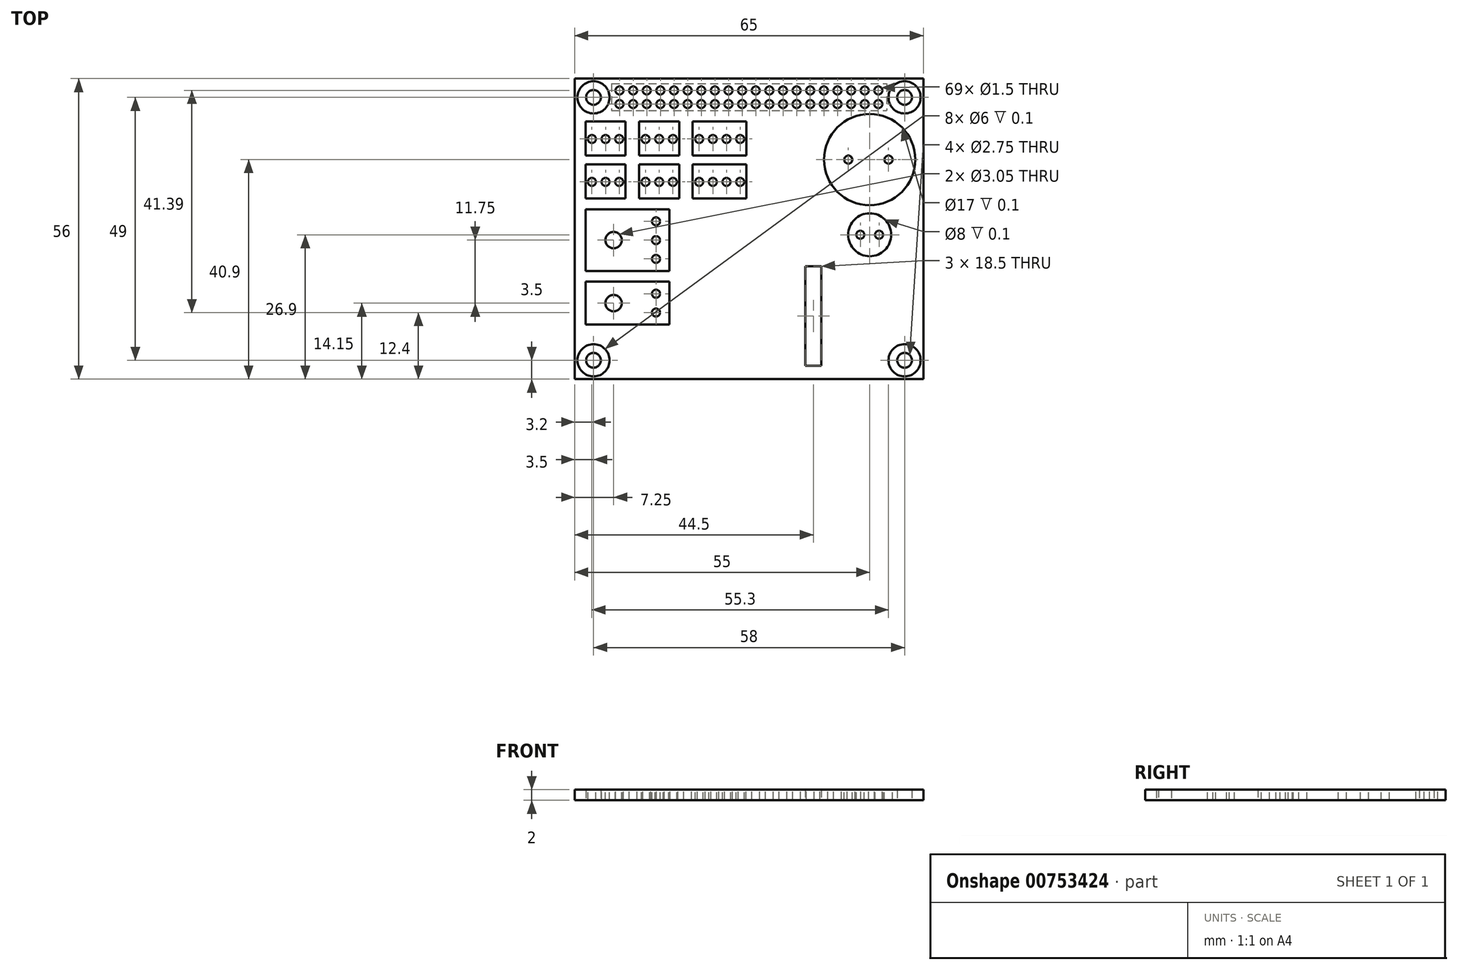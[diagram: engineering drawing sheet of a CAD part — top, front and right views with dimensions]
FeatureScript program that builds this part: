
annotation { "Feature Type Name" : "Feature", "Feature Type Description" : "" }
export const myFeature = defineFeature(function(context is Context, id is Id, definition is map)
    precondition{}
    {
        {
            var Q0;
            Q0=qCreatedBy(makeId("Top.planeOp"),FACE);
            var sketch = newSketch(context, id + "F0", { "sketchPlane" : qUnion([Q0])});
            skLineSegment(sketch, "E0.bottom", {"start": v(-32.5, 28) * mm, "end": v(52.5, 28) * mm});
            skLineSegment(sketch, "E0.top", {"start": v(-32.5, -28) * mm, "end": v(52.5, -28) * mm});
            skLineSegment(sketch, "E0.left", {"start": v(-32.5, 28) * mm, "end": v(-32.5, -28) * mm});
            skLineSegment(sketch, "E0.right", {"start": v(52.5, 28) * mm, "end": v(52.5, -28) * mm});
            skCircle(sketch, "E1", {"center": v(-29, 24.5) * mm, "radius": 1.38 * mm});
            skCircle(sketch, "E2", {"center": v(-29, -24.5) * mm, "radius": 1.38 * mm});
            skCircle(sketch, "E3", {"center": v(29, 24.5) * mm, "radius": 1.38 * mm});
            skCircle(sketch, "E4", {"center": v(29, -24.5) * mm, "radius": 1.38 * mm});
            skCircle(sketch, "E5", {"center": v(-29, -24.5) * mm, "radius": 3 * mm});
            skCircle(sketch, "E6", {"center": v(-29, 24.5) * mm, "radius": 3 * mm});
            skCircle(sketch, "E7", {"center": v(29, 24.5) * mm, "radius": 3 * mm});
            skCircle(sketch, "E8", {"center": v(29, -24.5) * mm, "radius": 3 * mm});
            skLineSegment(sketch, "E9", {"start": v(32.5, 28) * mm, "end": v(32.5, -28) * mm});
            skLineSegment(sketch, "E10.bottom", {"start": v(10.5, -7) * mm, "end": v(13.5, -7) * mm});
            skLineSegment(sketch, "E10.top", {"start": v(10.5, -25.5) * mm, "end": v(13.5, -25.5) * mm});
            skLineSegment(sketch, "E10.left", {"start": v(10.5, -7) * mm, "end": v(10.5, -25.5) * mm});
            skLineSegment(sketch, "E10.right", {"start": v(13.5, -7) * mm, "end": v(13.5, -25.5) * mm});
            skSolve(sketch);
        }
        {
            var Q0;
            {var subQ0=sQuery(id+"F0.wireOp",EDGE,"E0.left");Q0=makeQuery(id+"F0.imprint","IMPRINT",FACE,{"disambiguationData":[TD([[makeQuery(id+"F0.imprint","IMPRINT",EDGE,{"derivedFrom":subQ0}),1.0]])]});}
            extrude(context, id + "F1", {"entities" : qUnion([Q0]), "depth" : 1 * mm, "offsetDistance" : 25 * mm, "hasSecondDirection" : true, "secondDirectionOppositeDirection" : true, "secondDirectionDepth" : 1 * mm});
        }
        {
            var Q0;
            Q0=qCreatedBy(makeId("Top.planeOp"),FACE);
            var sketch = newSketch(context, id + "F2", { "sketchPlane" : qUnion([Q0])});
            skLineSegment(sketch, "E11.bottom", {"start": v(-32.5, 28) * mm, "end": v(52.5, 28) * mm});
            skLineSegment(sketch, "E11.top", {"start": v(-32.5, -28) * mm, "end": v(52.5, -28) * mm});
            skLineSegment(sketch, "E11.left", {"start": v(-32.5, 28) * mm, "end": v(-32.5, -28) * mm});
            skLineSegment(sketch, "E11.right", {"start": v(52.5, 28) * mm, "end": v(52.5, -28) * mm});
            skCircle(sketch, "E12", {"center": v(-29, 24.5) * mm, "radius": 1.38 * mm});
            skCircle(sketch, "E13", {"center": v(-29, -24.5) * mm, "radius": 1.38 * mm});
            skCircle(sketch, "E14", {"center": v(29, 24.5) * mm, "radius": 1.38 * mm});
            skCircle(sketch, "E15", {"center": v(29, -24.5) * mm, "radius": 1.38 * mm});
            skCircle(sketch, "E16", {"center": v(-29, -24.5) * mm, "radius": 3 * mm});
            skCircle(sketch, "E17", {"center": v(-29, 24.5) * mm, "radius": 3 * mm});
            skCircle(sketch, "E18", {"center": v(29, 24.5) * mm, "radius": 3 * mm});
            skCircle(sketch, "E19", {"center": v(29, -24.5) * mm, "radius": 3 * mm});
            skLineSegment(sketch, "E20", {"start": v(32.5, 28) * mm, "end": v(32.5, -28) * mm});
            skSolve(sketch);
        }
        {
            var Q0;
            Q0=makeQuery(id+"F2.imprint","IMPRINT",FACE,{"disambiguationData":[TD([[makeQuery(id+"F2.imprint","IMPRINT",EDGE,{"derivedFrom":sQuery(id+"F2.wireOp",EDGE,"E12")}),-1.0]])]});
            var Q1;
            Q1=makeQuery(id+"F2.imprint","IMPRINT",FACE,{"disambiguationData":[TD([[makeQuery(id+"F2.imprint","IMPRINT",EDGE,{"derivedFrom":sQuery(id+"F2.wireOp",EDGE,"E14")}),-1.0]])]});
            var Q2;
            Q2=makeQuery(id+"F2.imprint","IMPRINT",FACE,{"disambiguationData":[TD([[makeQuery(id+"F2.imprint","IMPRINT",EDGE,{"derivedFrom":sQuery(id+"F2.wireOp",EDGE,"E15")}),-1.0]])]});
            var Q3;
            Q3=makeQuery(id+"F2.imprint","IMPRINT",FACE,{"disambiguationData":[TD([[makeQuery(id+"F2.imprint","IMPRINT",EDGE,{"derivedFrom":sQuery(id+"F2.wireOp",EDGE,"E13")}),-1.0]])]});
            var Q4;
            Q4=makeQuery(id+"F1.opExtrude","CAP_FACE",FACE,{"disambiguationData":[OSD([sQuery(id+"F0.wireOp",EDGE,"E0.bottom"),sQuery(id+"F0.wireOp",EDGE,"E0.top"),sQuery(id+"F0.wireOp",EDGE,"E0.left"),sQuery(id+"F0.wireOp",EDGE,"E5"),sQuery(id+"F0.wireOp",EDGE,"E6"),sQuery(id+"F0.wireOp",EDGE,"E7"),sQuery(id+"F0.wireOp",EDGE,"E8"),sQuery(id+"F0.wireOp",EDGE,"E9")])],"isStart":false});
            var Q5;
            Q5=makeQuery(id+"F1.opExtrude","CAP_FACE",FACE,{"disambiguationData":[OSD([sQuery(id+"F0.wireOp",EDGE,"E0.bottom"),sQuery(id+"F0.wireOp",EDGE,"E0.top"),sQuery(id+"F0.wireOp",EDGE,"E0.left"),sQuery(id+"F0.wireOp",EDGE,"E5"),sQuery(id+"F0.wireOp",EDGE,"E6"),sQuery(id+"F0.wireOp",EDGE,"E7"),sQuery(id+"F0.wireOp",EDGE,"E8"),sQuery(id+"F0.wireOp",EDGE,"E9")])],"isStart":true});
            extrude(context, id + "F3", {"entities" : qUnion([Q0, Q1, Q2, Q3]), "operationType" : NewBodyOperationType.ADD, "endBound" : BoundingType.UP_TO_SURFACE, "depth" : 1.4 * mm, "endBoundEntityFace" : qUnion([Q4]), "hasOffset" : true, "offsetDistance" : 0.1 * mm, "hasSecondDirection" : true, "secondDirectionBound" : BoundingType.UP_TO_SURFACE, "secondDirectionOppositeDirection" : true, "secondDirectionDepth" : 1.4 * mm, "secondDirectionBoundEntityFace" : qUnion([Q5]), "hasSecondDirectionOffset" : true, "secondDirectionOffsetDistance" : 0.1 * mm});
        }
        {
            var Q0;
            Q0=makeQuery(id+"F1.opExtrude","CAP_FACE",FACE,{"disambiguationData":[OSD([sQuery(id+"F0.wireOp",EDGE,"E0.bottom"),sQuery(id+"F0.wireOp",EDGE,"E0.top"),sQuery(id+"F0.wireOp",EDGE,"E0.left"),sQuery(id+"F0.wireOp",EDGE,"E5"),sQuery(id+"F0.wireOp",EDGE,"E6"),sQuery(id+"F0.wireOp",EDGE,"E7"),sQuery(id+"F0.wireOp",EDGE,"E8"),sQuery(id+"F0.wireOp",EDGE,"E9"),sQuery(id+"F0.wireOp",EDGE,"E10.bottom"),sQuery(id+"F0.wireOp",EDGE,"E10.top"),sQuery(id+"F0.wireOp",EDGE,"E10.left"),sQuery(id+"F0.wireOp",EDGE,"E10.right")])],"isStart":false});
            var sketch = newSketch(context, id + "F4", { "sketchPlane" : qUnion([Q0])});
            skLineSegment(sketch, "E21.bottom", {"start": v(-30.5, 20) * mm, "end": v(-23.03, 20) * mm});
            skLineSegment(sketch, "E21.top", {"start": v(-30.5, 13.65) * mm, "end": v(-23.03, 13.65) * mm});
            skLineSegment(sketch, "E21.left", {"start": v(-30.5, 20) * mm, "end": v(-30.5, 13.65) * mm});
            skLineSegment(sketch, "E21.right", {"start": v(-23.03, 20) * mm, "end": v(-23.03, 13.65) * mm});
            skLineSegment(sketch, "E22.bottom", {"start": v(-30.5, 3.65) * mm, "end": v(-14.84, 3.65) * mm});
            skLineSegment(sketch, "E22.top", {"start": v(-30.5, -7.85) * mm, "end": v(-14.84, -7.85) * mm});
            skLineSegment(sketch, "E22.left", {"start": v(-30.5, 3.65) * mm, "end": v(-30.5, -7.85) * mm});
            skLineSegment(sketch, "E22.right", {"start": v(-14.84, 3.65) * mm, "end": v(-14.84, -7.85) * mm});
            skCircle(sketch, "E23", {"center": v(22.5, 12.9) * mm, "radius": 8.5 * mm});
            skLineSegment(sketch, "E24.bottom", {"start": v(-25.65, 22) * mm, "end": v(25.65, 22) * mm});
            skLineSegment(sketch, "E24.top", {"start": v(-25.65, 27) * mm, "end": v(25.65, 27) * mm});
            skLineSegment(sketch, "E24.left", {"start": v(-25.65, 22) * mm, "end": v(-25.65, 27) * mm});
            skLineSegment(sketch, "E24.right", {"start": v(25.65, 22) * mm, "end": v(25.65, 27) * mm});
            skLineSegment(sketch, "E25", {"start": v(0, 27) * mm, "end": v(0, 22) * mm, "construction": true});
            skPoint(sketch, "E26", {"position": v(-29, 24.5) * mm});
            skLineSegment(sketch, "E27", {"start": v(-25.65, 24.5) * mm, "end": v(25.65, 24.5) * mm, "construction": true});
            skCircle(sketch, "E28", {"center": v(24.1, 25.8) * mm, "radius": 0.75 * mm});
            skCircle(sketch, "E29", {"center": v(24.1, 23.25) * mm, "radius": 0.75 * mm});
            skCircle(sketch, "E30.1.0.0", {"center": v(21.57, 25.8) * mm, "radius": 0.75 * mm});
            skCircle(sketch, "E30.1.0.1", {"center": v(21.57, 23.25) * mm, "radius": 0.75 * mm});
            skCircle(sketch, "E30.2.0.0", {"center": v(19.03, 25.8) * mm, "radius": 0.75 * mm});
            skCircle(sketch, "E30.2.0.1", {"center": v(19.03, 23.25) * mm, "radius": 0.75 * mm});
            skCircle(sketch, "E30.3.0.0", {"center": v(16.49, 25.8) * mm, "radius": 0.75 * mm});
            skCircle(sketch, "E30.3.0.1", {"center": v(16.49, 23.25) * mm, "radius": 0.75 * mm});
            skCircle(sketch, "E30.4.0.0", {"center": v(13.95, 25.8) * mm, "radius": 0.75 * mm});
            skCircle(sketch, "E30.4.0.1", {"center": v(13.95, 23.25) * mm, "radius": 0.75 * mm});
            skCircle(sketch, "E30.5.0.0", {"center": v(11.4, 25.8) * mm, "radius": 0.75 * mm});
            skCircle(sketch, "E30.5.0.1", {"center": v(11.4, 23.25) * mm, "radius": 0.75 * mm});
            skCircle(sketch, "E30.6.0.0", {"center": v(8.87, 25.8) * mm, "radius": 0.75 * mm});
            skCircle(sketch, "E30.6.0.1", {"center": v(8.87, 23.25) * mm, "radius": 0.75 * mm});
            skCircle(sketch, "E30.7.0.0", {"center": v(6.33, 25.8) * mm, "radius": 0.75 * mm});
            skCircle(sketch, "E30.7.0.1", {"center": v(6.33, 23.25) * mm, "radius": 0.75 * mm});
            skCircle(sketch, "E30.8.0.0", {"center": v(3.79, 25.8) * mm, "radius": 0.75 * mm});
            skCircle(sketch, "E30.8.0.1", {"center": v(3.79, 23.25) * mm, "radius": 0.75 * mm});
            skCircle(sketch, "E30.9.0.0", {"center": v(1.25, 25.8) * mm, "radius": 0.75 * mm});
            skCircle(sketch, "E30.9.0.1", {"center": v(1.25, 23.25) * mm, "radius": 0.75 * mm});
            skCircle(sketch, "E30.10.0.0", {"center": v(-1.3, 25.8) * mm, "radius": 0.75 * mm});
            skCircle(sketch, "E30.10.0.1", {"center": v(-1.3, 23.25) * mm, "radius": 0.75 * mm});
            skCircle(sketch, "E30.11.0.0", {"center": v(-3.83, 25.8) * mm, "radius": 0.75 * mm});
            skCircle(sketch, "E30.11.0.1", {"center": v(-3.83, 23.25) * mm, "radius": 0.75 * mm});
            skCircle(sketch, "E30.12.0.0", {"center": v(-6.37, 25.8) * mm, "radius": 0.75 * mm});
            skCircle(sketch, "E30.12.0.1", {"center": v(-6.37, 23.25) * mm, "radius": 0.75 * mm});
            skCircle(sketch, "E30.13.0.0", {"center": v(-8.91, 25.8) * mm, "radius": 0.75 * mm});
            skCircle(sketch, "E30.13.0.1", {"center": v(-8.91, 23.25) * mm, "radius": 0.75 * mm});
            skCircle(sketch, "E30.14.0.0", {"center": v(-11.45, 25.8) * mm, "radius": 0.75 * mm});
            skCircle(sketch, "E30.14.0.1", {"center": v(-11.45, 23.25) * mm, "radius": 0.75 * mm});
            skCircle(sketch, "E30.15.0.0", {"center": v(-14, 25.8) * mm, "radius": 0.75 * mm});
            skCircle(sketch, "E30.15.0.1", {"center": v(-14, 23.25) * mm, "radius": 0.75 * mm});
            skCircle(sketch, "E30.16.0.0", {"center": v(-16.53, 25.8) * mm, "radius": 0.75 * mm});
            skCircle(sketch, "E30.16.0.1", {"center": v(-16.53, 23.25) * mm, "radius": 0.75 * mm});
            skCircle(sketch, "E30.17.0.0", {"center": v(-19.07, 25.8) * mm, "radius": 0.75 * mm});
            skCircle(sketch, "E30.17.0.1", {"center": v(-19.07, 23.25) * mm, "radius": 0.75 * mm});
            skCircle(sketch, "E30.18.0.0", {"center": v(-21.61, 25.8) * mm, "radius": 0.75 * mm});
            skCircle(sketch, "E30.18.0.1", {"center": v(-21.61, 23.25) * mm, "radius": 0.75 * mm});
            skCircle(sketch, "E30.19.0.0", {"center": v(-24.15, 25.8) * mm, "radius": 0.75 * mm});
            skCircle(sketch, "E30.19.0.1", {"center": v(-24.15, 23.25) * mm, "radius": 0.75 * mm});
            skLineSegment(sketch, "E30.direction1", {"start": v(24.1, 25.8) * mm, "end": v(21.57, 25.8) * mm, "construction": true});
            skLineSegment(sketch, "E31.bottom", {"start": v(-29.62, 17.07) * mm, "end": v(-28.98, 17.07) * mm});
            skLineSegment(sketch, "E31.top", {"start": v(-29.62, 16.43) * mm, "end": v(-28.98, 16.43) * mm});
            skLineSegment(sketch, "E31.left", {"start": v(-29.62, 17.07) * mm, "end": v(-29.62, 16.43) * mm});
            skLineSegment(sketch, "E31.right", {"start": v(-28.98, 17.07) * mm, "end": v(-28.98, 16.43) * mm});
            skLineSegment(sketch, "E32.bottom", {"start": v(-27.07, 17.07) * mm, "end": v(-26.43, 17.07) * mm});
            skLineSegment(sketch, "E32.top", {"start": v(-27.07, 16.43) * mm, "end": v(-26.43, 16.43) * mm});
            skLineSegment(sketch, "E32.left", {"start": v(-27.07, 17.07) * mm, "end": v(-27.07, 16.43) * mm});
            skLineSegment(sketch, "E32.right", {"start": v(-26.43, 17.07) * mm, "end": v(-26.43, 16.43) * mm});
            skLineSegment(sketch, "E33.bottom", {"start": v(-24.52, 17.07) * mm, "end": v(-23.88, 17.07) * mm});
            skLineSegment(sketch, "E33.top", {"start": v(-24.52, 16.43) * mm, "end": v(-23.88, 16.43) * mm});
            skLineSegment(sketch, "E33.left", {"start": v(-24.52, 17.07) * mm, "end": v(-24.52, 16.43) * mm});
            skLineSegment(sketch, "E33.right", {"start": v(-23.88, 17.07) * mm, "end": v(-23.88, 16.43) * mm});
            skCircle(sketch, "E34", {"center": v(-29.3, 16.75) * mm, "radius": 0.75 * mm});
            skPoint(sketch, "E34.centerSnap0", {"position": v(-28.98, 16.75) * mm});
            skPoint(sketch, "E34.centerSnap1", {"position": v(-29.3, 17.07) * mm});
            skCircle(sketch, "E35", {"center": v(-26.75, 16.75) * mm, "radius": 0.75 * mm});
            skPoint(sketch, "E35.centerSnap0", {"position": v(-26.43, 16.75) * mm});
            skPoint(sketch, "E35.centerSnap1", {"position": v(-26.75, 17.07) * mm});
            skCircle(sketch, "E36", {"center": v(-24.2, 16.75) * mm, "radius": 0.75 * mm});
            skPoint(sketch, "E36.centerSnap0", {"position": v(-23.88, 16.75) * mm});
            skPoint(sketch, "E36.centerSnap1", {"position": v(-24.2, 17.07) * mm});
            skLineSegment(sketch, "E37", {"start": v(-29.62, 16.43) * mm, "end": v(-23.88, 16.43) * mm, "construction": true});
            skPoint(sketch, "E38.0.1.0", {"position": v(-29.3, 9.07) * mm});
            skPoint(sketch, "E38.0.1.1", {"position": v(-23.88, 8.75) * mm});
            skPoint(sketch, "E38.0.1.2", {"position": v(-28.98, 8.75) * mm});
            skLineSegment(sketch, "E38.0.1.3", {"start": v(-29.62, 8.43) * mm, "end": v(-23.88, 8.43) * mm, "construction": true});
            skPoint(sketch, "E38.0.1.4", {"position": v(-24.2, 9.07) * mm});
            skPoint(sketch, "E38.0.1.5", {"position": v(-26.75, 9.07) * mm});
            skLineSegment(sketch, "E38.0.1.6", {"start": v(-30.5, 12) * mm, "end": v(-23.03, 12) * mm});
            skLineSegment(sketch, "E38.0.1.7", {"start": v(-30.5, 5.65) * mm, "end": v(-23.03, 5.65) * mm});
            skLineSegment(sketch, "E38.0.1.8", {"start": v(-30.5, 12) * mm, "end": v(-30.5, 5.65) * mm});
            skLineSegment(sketch, "E38.0.1.9", {"start": v(-23.03, 12) * mm, "end": v(-23.03, 5.65) * mm});
            skPoint(sketch, "E38.0.1.10", {"position": v(-26.43, 8.75) * mm});
            skLineSegment(sketch, "E38.0.1.11", {"start": v(-24.52, 9.07) * mm, "end": v(-23.88, 9.07) * mm});
            skLineSegment(sketch, "E38.0.1.12", {"start": v(-27.07, 9.07) * mm, "end": v(-27.07, 8.43) * mm});
            skLineSegment(sketch, "E38.0.1.13", {"start": v(-29.62, 8.43) * mm, "end": v(-28.98, 8.43) * mm});
            skLineSegment(sketch, "E38.0.1.14", {"start": v(-24.52, 9.07) * mm, "end": v(-24.52, 8.43) * mm});
            skCircle(sketch, "E38.0.1.15", {"center": v(-29.3, 8.75) * mm, "radius": 0.75 * mm});
            skLineSegment(sketch, "E38.0.1.16", {"start": v(-24.52, 8.43) * mm, "end": v(-23.88, 8.43) * mm});
            skLineSegment(sketch, "E38.0.1.17", {"start": v(-26.43, 9.07) * mm, "end": v(-26.43, 8.43) * mm});
            skLineSegment(sketch, "E38.0.1.18", {"start": v(-29.62, 9.07) * mm, "end": v(-28.98, 9.07) * mm});
            skLineSegment(sketch, "E38.0.1.19", {"start": v(-28.98, 9.07) * mm, "end": v(-28.98, 8.43) * mm});
            skLineSegment(sketch, "E38.0.1.20", {"start": v(-29.62, 9.07) * mm, "end": v(-29.62, 8.43) * mm});
            skLineSegment(sketch, "E38.0.1.21", {"start": v(-23.88, 9.07) * mm, "end": v(-23.88, 8.43) * mm});
            skCircle(sketch, "E38.0.1.22", {"center": v(-26.75, 8.75) * mm, "radius": 0.75 * mm});
            skLineSegment(sketch, "E38.0.1.23", {"start": v(-27.07, 9.07) * mm, "end": v(-26.43, 9.07) * mm});
            skLineSegment(sketch, "E38.0.1.24", {"start": v(-27.07, 8.43) * mm, "end": v(-26.43, 8.43) * mm});
            skCircle(sketch, "E38.0.1.25", {"center": v(-24.2, 8.75) * mm, "radius": 0.75 * mm});
            skPoint(sketch, "E38.1.0.0", {"position": v(-19.3, 17.07) * mm});
            skPoint(sketch, "E38.1.0.1", {"position": v(-13.88, 16.75) * mm});
            skPoint(sketch, "E38.1.0.2", {"position": v(-18.98, 16.75) * mm});
            skLineSegment(sketch, "E38.1.0.3", {"start": v(-19.62, 16.43) * mm, "end": v(-13.88, 16.43) * mm, "construction": true});
            skPoint(sketch, "E38.1.0.4", {"position": v(-14.2, 17.07) * mm});
            skPoint(sketch, "E38.1.0.5", {"position": v(-16.75, 17.07) * mm});
            skLineSegment(sketch, "E38.1.0.6", {"start": v(-20.5, 20) * mm, "end": v(-13.03, 20) * mm});
            skLineSegment(sketch, "E38.1.0.7", {"start": v(-20.5, 13.65) * mm, "end": v(-13.03, 13.65) * mm});
            skLineSegment(sketch, "E38.1.0.8", {"start": v(-20.5, 20) * mm, "end": v(-20.5, 13.65) * mm});
            skLineSegment(sketch, "E38.1.0.9", {"start": v(-13.03, 20) * mm, "end": v(-13.03, 13.65) * mm});
            skPoint(sketch, "E38.1.0.10", {"position": v(-16.43, 16.75) * mm});
            skLineSegment(sketch, "E38.1.0.11", {"start": v(-14.52, 17.07) * mm, "end": v(-13.88, 17.07) * mm});
            skLineSegment(sketch, "E38.1.0.12", {"start": v(-17.07, 17.07) * mm, "end": v(-17.07, 16.43) * mm});
            skLineSegment(sketch, "E38.1.0.13", {"start": v(-19.62, 16.43) * mm, "end": v(-18.98, 16.43) * mm});
            skLineSegment(sketch, "E38.1.0.14", {"start": v(-14.52, 17.07) * mm, "end": v(-14.52, 16.43) * mm});
            skCircle(sketch, "E38.1.0.15", {"center": v(-19.3, 16.75) * mm, "radius": 0.75 * mm});
            skLineSegment(sketch, "E38.1.0.16", {"start": v(-14.52, 16.43) * mm, "end": v(-13.88, 16.43) * mm});
            skLineSegment(sketch, "E38.1.0.17", {"start": v(-16.43, 17.07) * mm, "end": v(-16.43, 16.43) * mm});
            skLineSegment(sketch, "E38.1.0.18", {"start": v(-19.62, 17.07) * mm, "end": v(-18.98, 17.07) * mm});
            skLineSegment(sketch, "E38.1.0.19", {"start": v(-18.98, 17.07) * mm, "end": v(-18.98, 16.43) * mm});
            skLineSegment(sketch, "E38.1.0.20", {"start": v(-19.62, 17.07) * mm, "end": v(-19.62, 16.43) * mm});
            skLineSegment(sketch, "E38.1.0.21", {"start": v(-13.88, 17.07) * mm, "end": v(-13.88, 16.43) * mm});
            skCircle(sketch, "E38.1.0.22", {"center": v(-16.75, 16.75) * mm, "radius": 0.75 * mm});
            skLineSegment(sketch, "E38.1.0.23", {"start": v(-17.07, 17.07) * mm, "end": v(-16.43, 17.07) * mm});
            skLineSegment(sketch, "E38.1.0.24", {"start": v(-17.07, 16.43) * mm, "end": v(-16.43, 16.43) * mm});
            skCircle(sketch, "E38.1.0.25", {"center": v(-14.2, 16.75) * mm, "radius": 0.75 * mm});
            skPoint(sketch, "E38.1.1.0", {"position": v(-19.3, 9.07) * mm});
            skPoint(sketch, "E38.1.1.1", {"position": v(-13.88, 8.75) * mm});
            skPoint(sketch, "E38.1.1.2", {"position": v(-18.98, 8.75) * mm});
            skLineSegment(sketch, "E38.1.1.3", {"start": v(-19.62, 8.43) * mm, "end": v(-13.88, 8.43) * mm, "construction": true});
            skPoint(sketch, "E38.1.1.4", {"position": v(-14.2, 9.07) * mm});
            skPoint(sketch, "E38.1.1.5", {"position": v(-16.75, 9.07) * mm});
            skLineSegment(sketch, "E38.1.1.6", {"start": v(-20.5, 12) * mm, "end": v(-13.03, 12) * mm});
            skLineSegment(sketch, "E38.1.1.7", {"start": v(-20.5, 5.65) * mm, "end": v(-13.03, 5.65) * mm});
            skLineSegment(sketch, "E38.1.1.8", {"start": v(-20.5, 12) * mm, "end": v(-20.5, 5.65) * mm});
            skLineSegment(sketch, "E38.1.1.9", {"start": v(-13.03, 12) * mm, "end": v(-13.03, 5.65) * mm});
            skPoint(sketch, "E38.1.1.10", {"position": v(-16.43, 8.75) * mm});
            skLineSegment(sketch, "E38.1.1.11", {"start": v(-14.52, 9.07) * mm, "end": v(-13.88, 9.07) * mm});
            skLineSegment(sketch, "E38.1.1.12", {"start": v(-17.07, 9.07) * mm, "end": v(-17.07, 8.43) * mm});
            skLineSegment(sketch, "E38.1.1.13", {"start": v(-19.62, 8.43) * mm, "end": v(-18.98, 8.43) * mm});
            skLineSegment(sketch, "E38.1.1.14", {"start": v(-14.52, 9.07) * mm, "end": v(-14.52, 8.43) * mm});
            skCircle(sketch, "E38.1.1.15", {"center": v(-19.3, 8.75) * mm, "radius": 0.75 * mm});
            skLineSegment(sketch, "E38.1.1.16", {"start": v(-14.52, 8.43) * mm, "end": v(-13.88, 8.43) * mm});
            skLineSegment(sketch, "E38.1.1.17", {"start": v(-16.43, 9.07) * mm, "end": v(-16.43, 8.43) * mm});
            skLineSegment(sketch, "E38.1.1.18", {"start": v(-19.62, 9.07) * mm, "end": v(-18.98, 9.07) * mm});
            skLineSegment(sketch, "E38.1.1.19", {"start": v(-18.98, 9.07) * mm, "end": v(-18.98, 8.43) * mm});
            skLineSegment(sketch, "E38.1.1.20", {"start": v(-19.62, 9.07) * mm, "end": v(-19.62, 8.43) * mm});
            skLineSegment(sketch, "E38.1.1.21", {"start": v(-13.88, 9.07) * mm, "end": v(-13.88, 8.43) * mm});
            skCircle(sketch, "E38.1.1.22", {"center": v(-16.75, 8.75) * mm, "radius": 0.75 * mm});
            skLineSegment(sketch, "E38.1.1.23", {"start": v(-17.07, 9.07) * mm, "end": v(-16.43, 9.07) * mm});
            skLineSegment(sketch, "E38.1.1.24", {"start": v(-17.07, 8.43) * mm, "end": v(-16.43, 8.43) * mm});
            skCircle(sketch, "E38.1.1.25", {"center": v(-14.2, 8.75) * mm, "radius": 0.75 * mm});
            skLineSegment(sketch, "E38.direction1", {"start": v(-30.5, 13.65) * mm, "end": v(-20.5, 13.65) * mm, "construction": true});
            skLineSegment(sketch, "E38.direction2", {"start": v(-30.5, 13.65) * mm, "end": v(-30.5, 5.65) * mm, "construction": true});
            skLineSegment(sketch, "E39.bottom", {"start": v(-10.5, 20) * mm, "end": v(-0.5, 20) * mm});
            skLineSegment(sketch, "E39.top", {"start": v(-10.5, 13.65) * mm, "end": v(-0.5, 13.65) * mm});
            skLineSegment(sketch, "E39.left", {"start": v(-10.5, 20) * mm, "end": v(-10.5, 13.65) * mm});
            skLineSegment(sketch, "E39.right", {"start": v(-0.5, 20) * mm, "end": v(-0.5, 13.65) * mm});
            skLineSegment(sketch, "E40.bottom", {"start": v(-9.62, 17.07) * mm, "end": v(-8.98, 17.07) * mm});
            skLineSegment(sketch, "E40.top", {"start": v(-9.62, 16.43) * mm, "end": v(-8.98, 16.43) * mm});
            skLineSegment(sketch, "E40.left", {"start": v(-9.62, 17.07) * mm, "end": v(-9.62, 16.43) * mm});
            skLineSegment(sketch, "E40.right", {"start": v(-8.98, 17.07) * mm, "end": v(-8.98, 16.43) * mm});
            skLineSegment(sketch, "E41.bottom", {"start": v(-7.07, 17.07) * mm, "end": v(-6.43, 17.07) * mm});
            skLineSegment(sketch, "E41.top", {"start": v(-7.07, 16.43) * mm, "end": v(-6.43, 16.43) * mm});
            skLineSegment(sketch, "E41.left", {"start": v(-7.07, 17.07) * mm, "end": v(-7.07, 16.43) * mm});
            skLineSegment(sketch, "E41.right", {"start": v(-6.43, 17.07) * mm, "end": v(-6.43, 16.43) * mm});
            skLineSegment(sketch, "E42.bottom", {"start": v(-4.52, 17.07) * mm, "end": v(-3.88, 17.07) * mm});
            skLineSegment(sketch, "E42.top", {"start": v(-4.52, 16.43) * mm, "end": v(-3.88, 16.43) * mm});
            skLineSegment(sketch, "E42.left", {"start": v(-4.52, 17.07) * mm, "end": v(-4.52, 16.43) * mm});
            skLineSegment(sketch, "E42.right", {"start": v(-3.88, 17.07) * mm, "end": v(-3.88, 16.43) * mm});
            skCircle(sketch, "E43", {"center": v(-9.3, 16.75) * mm, "radius": 0.75 * mm});
            skPoint(sketch, "E43.centerSnap0", {"position": v(-8.98, 16.75) * mm});
            skPoint(sketch, "E43.centerSnap1", {"position": v(-9.3, 17.07) * mm});
            skCircle(sketch, "E44", {"center": v(-6.75, 16.75) * mm, "radius": 0.75 * mm});
            skPoint(sketch, "E44.centerSnap0", {"position": v(-6.43, 16.75) * mm});
            skPoint(sketch, "E44.centerSnap1", {"position": v(-6.75, 17.07) * mm});
            skCircle(sketch, "E45", {"center": v(-4.2, 16.75) * mm, "radius": 0.75 * mm});
            skPoint(sketch, "E45.centerSnap0", {"position": v(-3.88, 16.75) * mm});
            skPoint(sketch, "E45.centerSnap1", {"position": v(-4.2, 17.07) * mm});
            skLineSegment(sketch, "E46", {"start": v(-9.62, 16.43) * mm, "end": v(-3.88, 16.43) * mm, "construction": true});
            skPoint(sketch, "E47.endSnap0", {"position": v(-4.2, 16.43) * mm});
            skLineSegment(sketch, "E48.bottom", {"start": v(-1.97, 17.07) * mm, "end": v(-1.33, 17.07) * mm});
            skLineSegment(sketch, "E48.top", {"start": v(-1.97, 16.43) * mm, "end": v(-1.33, 16.43) * mm});
            skLineSegment(sketch, "E48.left", {"start": v(-1.97, 17.07) * mm, "end": v(-1.97, 16.43) * mm});
            skLineSegment(sketch, "E48.right", {"start": v(-1.33, 17.07) * mm, "end": v(-1.33, 16.43) * mm});
            skCircle(sketch, "E49", {"center": v(-1.65, 16.75) * mm, "radius": 0.75 * mm});
            skPoint(sketch, "E49.centerSnap0", {"position": v(-1.33, 16.75) * mm});
            skPoint(sketch, "E49.centerSnap1", {"position": v(-1.65, 17.07) * mm});
            skLineSegment(sketch, "E50", {"start": v(-3.88, 16.43) * mm, "end": v(-1.33, 16.43) * mm, "construction": true});
            skPoint(sketch, "E51.0.1.0", {"position": v(-4.2, 9.07) * mm});
            skPoint(sketch, "E51.0.1.1", {"position": v(-9.3, 9.07) * mm});
            skPoint(sketch, "E51.0.1.2", {"position": v(-6.43, 8.75) * mm});
            skLineSegment(sketch, "E51.0.1.3", {"start": v(-10.5, 5.65) * mm, "end": v(-0.5, 5.65) * mm});
            skPoint(sketch, "E51.0.1.4", {"position": v(-1.33, 8.75) * mm});
            skCircle(sketch, "E51.0.1.5", {"center": v(-1.65, 8.75) * mm, "radius": 0.75 * mm});
            skLineSegment(sketch, "E51.0.1.6", {"start": v(-10.5, 12) * mm, "end": v(-0.5, 12) * mm});
            skPoint(sketch, "E51.0.1.7", {"position": v(-1.65, 9.07) * mm});
            skPoint(sketch, "E51.0.1.8", {"position": v(-4.2, 8.43) * mm});
            skPoint(sketch, "E51.0.1.9", {"position": v(-3.88, 8.75) * mm});
            skCircle(sketch, "E51.0.1.10", {"center": v(-9.3, 8.75) * mm, "radius": 0.75 * mm});
            skPoint(sketch, "E51.0.1.11", {"position": v(-6.75, 9.07) * mm});
            skPoint(sketch, "E51.0.1.12", {"position": v(-8.98, 8.75) * mm});
            skLineSegment(sketch, "E51.0.1.13", {"start": v(-9.62, 8.43) * mm, "end": v(-3.88, 8.43) * mm, "construction": true});
            skLineSegment(sketch, "E51.0.1.14", {"start": v(-10.5, 12) * mm, "end": v(-10.5, 5.65) * mm});
            skCircle(sketch, "E51.0.1.15", {"center": v(-4.2, 8.75) * mm, "radius": 0.75 * mm});
            skLineSegment(sketch, "E51.0.1.16", {"start": v(-3.88, 8.43) * mm, "end": v(-1.33, 8.43) * mm, "construction": true});
            skLineSegment(sketch, "E51.0.1.17", {"start": v(-0.5, 12) * mm, "end": v(-0.5, 5.65) * mm});
            skCircle(sketch, "E51.0.1.18", {"center": v(-6.75, 8.75) * mm, "radius": 0.75 * mm});
            skLineSegment(sketch, "E51.0.1.19", {"start": v(-4.52, 9.07) * mm, "end": v(-4.52, 8.43) * mm});
            skLineSegment(sketch, "E51.0.1.20", {"start": v(-7.07, 8.43) * mm, "end": v(-6.43, 8.43) * mm});
            skLineSegment(sketch, "E51.0.1.21", {"start": v(-7.07, 9.07) * mm, "end": v(-7.07, 8.43) * mm});
            skLineSegment(sketch, "E51.0.1.22", {"start": v(-9.62, 9.07) * mm, "end": v(-9.62, 8.43) * mm});
            skLineSegment(sketch, "E51.0.1.23", {"start": v(-6.43, 9.07) * mm, "end": v(-6.43, 8.43) * mm});
            skLineSegment(sketch, "E51.0.1.24", {"start": v(-7.07, 9.07) * mm, "end": v(-6.43, 9.07) * mm});
            skLineSegment(sketch, "E51.0.1.25", {"start": v(-1.97, 9.07) * mm, "end": v(-1.97, 8.43) * mm});
            skLineSegment(sketch, "E51.0.1.26", {"start": v(-1.33, 9.07) * mm, "end": v(-1.33, 8.43) * mm});
            skLineSegment(sketch, "E51.0.1.27", {"start": v(-1.97, 9.07) * mm, "end": v(-1.33, 9.07) * mm});
            skLineSegment(sketch, "E51.0.1.28", {"start": v(-9.62, 9.07) * mm, "end": v(-8.98, 9.07) * mm});
            skLineSegment(sketch, "E51.0.1.29", {"start": v(-1.97, 8.43) * mm, "end": v(-1.33, 8.43) * mm});
            skLineSegment(sketch, "E51.0.1.30", {"start": v(-9.62, 8.43) * mm, "end": v(-8.98, 8.43) * mm});
            skLineSegment(sketch, "E51.0.1.31", {"start": v(-4.52, 8.43) * mm, "end": v(-3.88, 8.43) * mm});
            skLineSegment(sketch, "E51.0.1.32", {"start": v(-8.98, 9.07) * mm, "end": v(-8.98, 8.43) * mm});
            skLineSegment(sketch, "E51.0.1.33", {"start": v(-4.52, 9.07) * mm, "end": v(-3.88, 9.07) * mm});
            skLineSegment(sketch, "E51.0.1.34", {"start": v(-3.88, 9.07) * mm, "end": v(-3.88, 8.43) * mm});
            skLineSegment(sketch, "E51.direction1", {"start": v(-10.5, 13.65) * mm, "end": v(0.98, 13.7) * mm, "construction": true});
            skLineSegment(sketch, "E51.direction2", {"start": v(-10.5, 13.65) * mm, "end": v(-10.5, 5.65) * mm, "construction": true});
            skCircle(sketch, "E52", {"center": v(-25.25, -2.1) * mm, "radius": 1.52 * mm});
            skPoint(sketch, "E52.centerSnap0", {"position": v(-30.5, -2.1) * mm});
            skCircle(sketch, "E53", {"center": v(-17.34, 1.4) * mm, "radius": 0.75 * mm});
            skCircle(sketch, "E54", {"center": v(-17.34, -2.1) * mm, "radius": 0.75 * mm});
            skCircle(sketch, "E55", {"center": v(-17.34, -5.6) * mm, "radius": 0.75 * mm});
            skLineSegment(sketch, "E56", {"start": v(-30.5, -2.1) * mm, "end": v(-14.84, -2.1) * mm, "construction": true});
            skLineSegment(sketch, "E57.bottom", {"start": v(-30.5, -9.85) * mm, "end": v(-14.84, -9.85) * mm});
            skLineSegment(sketch, "E57.top", {"start": v(-30.5, -17.85) * mm, "end": v(-14.84, -17.85) * mm});
            skLineSegment(sketch, "E57.left", {"start": v(-30.5, -9.85) * mm, "end": v(-30.5, -17.85) * mm});
            skLineSegment(sketch, "E57.right", {"start": v(-14.84, -9.85) * mm, "end": v(-14.84, -17.85) * mm});
            skCircle(sketch, "E58", {"center": v(-25.25, -13.85) * mm, "radius": 1.52 * mm});
            skPoint(sketch, "E58.centerSnap0", {"position": v(-30.5, -13.85) * mm});
            skCircle(sketch, "E59", {"center": v(-17.34, -12.1) * mm, "radius": 0.75 * mm});
            skCircle(sketch, "E60", {"center": v(-17.34, -13.85) * mm, "radius": 0.75 * mm, "construction": true});
            skCircle(sketch, "E61", {"center": v(-17.34, -15.6) * mm, "radius": 0.75 * mm});
            skLineSegment(sketch, "E62", {"start": v(-30.5, -13.85) * mm, "end": v(-14.84, -13.85) * mm, "construction": true});
            skCircle(sketch, "E63", {"center": v(18.5, 12.9) * mm, "radius": 0.75 * mm});
            skCircle(sketch, "E64", {"center": v(26, 12.9) * mm, "radius": 0.75 * mm});
            skCircle(sketch, "E65", {"center": v(22.5, -1.1) * mm, "radius": 4 * mm});
            skLineSegment(sketch, "E66", {"start": v(20.75, -1.1) * mm, "end": v(24.25, -1.1) * mm, "construction": true});
            skCircle(sketch, "E67", {"center": v(20.75, -1.1) * mm, "radius": 0.75 * mm});
            skCircle(sketch, "E68", {"center": v(24.25, -1.1) * mm, "radius": 0.75 * mm});
            skSolve(sketch);
        }
        {
            var Q0;
            Q0=makeQuery(id+"F4.imprint","IMPRINT",FACE,{"disambiguationData":[TD([[makeQuery(id+"F4.imprint","IMPRINT",EDGE,{"derivedFrom":sQuery(id+"F4.wireOp",EDGE,"E38.0.1.13")}),-1.0]])]});
            var Q1;
            Q1=makeQuery(id+"F4.imprint","IMPRINT",FACE,{"disambiguationData":[TD([[makeQuery(id+"F4.imprint","IMPRINT",EDGE,{"derivedFrom":sQuery(id+"F4.wireOp",EDGE,"E38.0.1.13")}),1.0]])]});
            var Q2;
            Q2=makeQuery(id+"F4.imprint","IMPRINT",FACE,{"disambiguationData":[TD([[makeQuery(id+"F4.imprint","IMPRINT",EDGE,{"derivedFrom":sQuery(id+"F4.wireOp",EDGE,"E38.0.1.12")}),-1.0]])]});
            var Q3;
            Q3=makeQuery(id+"F4.imprint","IMPRINT",FACE,{"disambiguationData":[TD([[makeQuery(id+"F4.imprint","IMPRINT",EDGE,{"derivedFrom":sQuery(id+"F4.wireOp",EDGE,"E38.0.1.12")}),1.0]])]});
            var Q4;
            Q4=makeQuery(id+"F4.imprint","IMPRINT",FACE,{"disambiguationData":[TD([[makeQuery(id+"F4.imprint","IMPRINT",EDGE,{"derivedFrom":sQuery(id+"F4.wireOp",EDGE,"E38.0.1.11")}),1.0]])]});
            var Q5;
            Q5=makeQuery(id+"F4.imprint","IMPRINT",FACE,{"disambiguationData":[TD([[makeQuery(id+"F4.imprint","IMPRINT",EDGE,{"derivedFrom":sQuery(id+"F4.wireOp",EDGE,"E38.0.1.11")}),-1.0]])]});
            var Q6;
            Q6=makeQuery(id+"F4.imprint","IMPRINT",FACE,{"disambiguationData":[TD([[makeQuery(id+"F4.imprint","IMPRINT",EDGE,{"derivedFrom":sQuery(id+"F4.wireOp",EDGE,"E31.bottom")}),1.0]])]});
            var Q7;
            Q7=makeQuery(id+"F4.imprint","IMPRINT",FACE,{"disambiguationData":[TD([[makeQuery(id+"F4.imprint","IMPRINT",EDGE,{"derivedFrom":sQuery(id+"F4.wireOp",EDGE,"E31.bottom")}),-1.0]])]});
            var Q8;
            Q8=makeQuery(id+"F4.imprint","IMPRINT",FACE,{"disambiguationData":[TD([[makeQuery(id+"F4.imprint","IMPRINT",EDGE,{"derivedFrom":sQuery(id+"F4.wireOp",EDGE,"E32.bottom")}),1.0]])]});
            var Q9;
            Q9=makeQuery(id+"F4.imprint","IMPRINT",FACE,{"disambiguationData":[TD([[makeQuery(id+"F4.imprint","IMPRINT",EDGE,{"derivedFrom":sQuery(id+"F4.wireOp",EDGE,"E32.bottom")}),-1.0]])]});
            var Q10;
            Q10=makeQuery(id+"F4.imprint","IMPRINT",FACE,{"disambiguationData":[TD([[makeQuery(id+"F4.imprint","IMPRINT",EDGE,{"derivedFrom":sQuery(id+"F4.wireOp",EDGE,"E33.bottom")}),1.0]])]});
            var Q11;
            Q11=makeQuery(id+"F4.imprint","IMPRINT",FACE,{"disambiguationData":[TD([[makeQuery(id+"F4.imprint","IMPRINT",EDGE,{"derivedFrom":sQuery(id+"F4.wireOp",EDGE,"E33.bottom")}),-1.0]])]});
            var Q12;
            Q12=makeQuery(id+"F4.imprint","IMPRINT",FACE,{"disambiguationData":[TD([[makeQuery(id+"F4.imprint","IMPRINT",EDGE,{"derivedFrom":sQuery(id+"F4.wireOp",EDGE,"E38.1.0.13")}),-1.0]])]});
            var Q13;
            Q13=makeQuery(id+"F4.imprint","IMPRINT",FACE,{"disambiguationData":[TD([[makeQuery(id+"F4.imprint","IMPRINT",EDGE,{"derivedFrom":sQuery(id+"F4.wireOp",EDGE,"E38.1.0.13")}),1.0]])]});
            var Q14;
            Q14=makeQuery(id+"F4.imprint","IMPRINT",FACE,{"disambiguationData":[TD([[makeQuery(id+"F4.imprint","IMPRINT",EDGE,{"derivedFrom":sQuery(id+"F4.wireOp",EDGE,"E38.1.0.12")}),-1.0]])]});
            var Q15;
            Q15=makeQuery(id+"F4.imprint","IMPRINT",FACE,{"disambiguationData":[TD([[makeQuery(id+"F4.imprint","IMPRINT",EDGE,{"derivedFrom":sQuery(id+"F4.wireOp",EDGE,"E38.1.0.12")}),1.0]])]});
            var Q16;
            Q16=makeQuery(id+"F4.imprint","IMPRINT",FACE,{"disambiguationData":[TD([[makeQuery(id+"F4.imprint","IMPRINT",EDGE,{"derivedFrom":sQuery(id+"F4.wireOp",EDGE,"E38.1.0.11")}),1.0]])]});
            var Q17;
            Q17=makeQuery(id+"F4.imprint","IMPRINT",FACE,{"disambiguationData":[TD([[makeQuery(id+"F4.imprint","IMPRINT",EDGE,{"derivedFrom":sQuery(id+"F4.wireOp",EDGE,"E38.1.0.11")}),-1.0]])]});
            var Q18;
            Q18=makeQuery(id+"F4.imprint","IMPRINT",FACE,{"disambiguationData":[TD([[makeQuery(id+"F4.imprint","IMPRINT",EDGE,{"derivedFrom":sQuery(id+"F4.wireOp",EDGE,"E40.bottom")}),1.0]])]});
            var Q19;
            Q19=makeQuery(id+"F4.imprint","IMPRINT",FACE,{"disambiguationData":[TD([[makeQuery(id+"F4.imprint","IMPRINT",EDGE,{"derivedFrom":sQuery(id+"F4.wireOp",EDGE,"E40.bottom")}),-1.0]])]});
            var Q20;
            Q20=makeQuery(id+"F4.imprint","IMPRINT",FACE,{"disambiguationData":[TD([[makeQuery(id+"F4.imprint","IMPRINT",EDGE,{"derivedFrom":sQuery(id+"F4.wireOp",EDGE,"E41.bottom")}),1.0]])]});
            var Q21;
            Q21=makeQuery(id+"F4.imprint","IMPRINT",FACE,{"disambiguationData":[TD([[makeQuery(id+"F4.imprint","IMPRINT",EDGE,{"derivedFrom":sQuery(id+"F4.wireOp",EDGE,"E41.bottom")}),-1.0]])]});
            var Q22;
            Q22=makeQuery(id+"F4.imprint","IMPRINT",FACE,{"disambiguationData":[TD([[makeQuery(id+"F4.imprint","IMPRINT",EDGE,{"derivedFrom":sQuery(id+"F4.wireOp",EDGE,"E42.bottom")}),1.0]])]});
            var Q23;
            Q23=makeQuery(id+"F4.imprint","IMPRINT",FACE,{"disambiguationData":[TD([[makeQuery(id+"F4.imprint","IMPRINT",EDGE,{"derivedFrom":sQuery(id+"F4.wireOp",EDGE,"E42.bottom")}),-1.0]])]});
            var Q24;
            Q24=makeQuery(id+"F4.imprint","IMPRINT",FACE,{"disambiguationData":[TD([[makeQuery(id+"F4.imprint","IMPRINT",EDGE,{"derivedFrom":sQuery(id+"F4.wireOp",EDGE,"E48.bottom")}),1.0]])]});
            var Q25;
            Q25=makeQuery(id+"F4.imprint","IMPRINT",FACE,{"disambiguationData":[TD([[makeQuery(id+"F4.imprint","IMPRINT",EDGE,{"derivedFrom":sQuery(id+"F4.wireOp",EDGE,"E48.bottom")}),-1.0]])]});
            var Q26;
            Q26=makeQuery(id+"F4.imprint","IMPRINT",FACE,{"disambiguationData":[TD([[makeQuery(id+"F4.imprint","IMPRINT",EDGE,{"derivedFrom":sQuery(id+"F4.wireOp",EDGE,"E51.0.1.10")}),1.0]])]});
            var Q27;
            Q27=makeQuery(id+"F4.imprint","IMPRINT",FACE,{"disambiguationData":[TD([[makeQuery(id+"F4.imprint","IMPRINT",EDGE,{"derivedFrom":sQuery(id+"F4.wireOp",EDGE,"E51.0.1.22")}),1.0]])]});
            var Q28;
            Q28=makeQuery(id+"F4.imprint","IMPRINT",FACE,{"disambiguationData":[TD([[makeQuery(id+"F4.imprint","IMPRINT",EDGE,{"derivedFrom":sQuery(id+"F4.wireOp",EDGE,"E51.0.1.18")}),1.0]])]});
            var Q29;
            Q29=makeQuery(id+"F4.imprint","IMPRINT",FACE,{"disambiguationData":[TD([[makeQuery(id+"F4.imprint","IMPRINT",EDGE,{"derivedFrom":sQuery(id+"F4.wireOp",EDGE,"E51.0.1.20")}),1.0]])]});
            var Q30;
            Q30=makeQuery(id+"F4.imprint","IMPRINT",FACE,{"disambiguationData":[TD([[makeQuery(id+"F4.imprint","IMPRINT",EDGE,{"derivedFrom":sQuery(id+"F4.wireOp",EDGE,"E51.0.1.15")}),1.0]])]});
            var Q31;
            Q31=makeQuery(id+"F4.imprint","IMPRINT",FACE,{"disambiguationData":[TD([[makeQuery(id+"F4.imprint","IMPRINT",EDGE,{"derivedFrom":sQuery(id+"F4.wireOp",EDGE,"E51.0.1.19")}),1.0]])]});
            var Q32;
            Q32=makeQuery(id+"F4.imprint","IMPRINT",FACE,{"disambiguationData":[TD([[makeQuery(id+"F4.imprint","IMPRINT",EDGE,{"derivedFrom":sQuery(id+"F4.wireOp",EDGE,"E51.0.1.5")}),1.0]])]});
            var Q33;
            Q33=makeQuery(id+"F4.imprint","IMPRINT",FACE,{"disambiguationData":[TD([[makeQuery(id+"F4.imprint","IMPRINT",EDGE,{"derivedFrom":sQuery(id+"F4.wireOp",EDGE,"E51.0.1.25")}),1.0]])]});
            var Q34;
            Q34=makeQuery(id+"F4.imprint","IMPRINT",FACE,{"disambiguationData":[TD([[makeQuery(id+"F4.imprint","IMPRINT",EDGE,{"derivedFrom":sQuery(id+"F4.wireOp",EDGE,"E38.1.1.11")}),1.0]])]});
            var Q35;
            Q35=makeQuery(id+"F4.imprint","IMPRINT",FACE,{"disambiguationData":[TD([[makeQuery(id+"F4.imprint","IMPRINT",EDGE,{"derivedFrom":sQuery(id+"F4.wireOp",EDGE,"E38.1.1.11")}),-1.0]])]});
            var Q36;
            Q36=makeQuery(id+"F4.imprint","IMPRINT",FACE,{"disambiguationData":[TD([[makeQuery(id+"F4.imprint","IMPRINT",EDGE,{"derivedFrom":sQuery(id+"F4.wireOp",EDGE,"E38.1.1.12")}),-1.0]])]});
            var Q37;
            Q37=makeQuery(id+"F4.imprint","IMPRINT",FACE,{"disambiguationData":[TD([[makeQuery(id+"F4.imprint","IMPRINT",EDGE,{"derivedFrom":sQuery(id+"F4.wireOp",EDGE,"E38.1.1.12")}),1.0]])]});
            var Q38;
            Q38=makeQuery(id+"F4.imprint","IMPRINT",FACE,{"disambiguationData":[TD([[makeQuery(id+"F4.imprint","IMPRINT",EDGE,{"derivedFrom":sQuery(id+"F4.wireOp",EDGE,"E38.1.1.13")}),-1.0]])]});
            var Q39;
            Q39=makeQuery(id+"F4.imprint","IMPRINT",FACE,{"disambiguationData":[TD([[makeQuery(id+"F4.imprint","IMPRINT",EDGE,{"derivedFrom":sQuery(id+"F4.wireOp",EDGE,"E38.1.1.13")}),1.0]])]});
            var Q40;
            Q40=makeQuery(id+"F4.imprint","IMPRINT",FACE,{"disambiguationData":[TD([[makeQuery(id+"F4.imprint","IMPRINT",EDGE,{"derivedFrom":sQuery(id+"F4.wireOp",EDGE,"E53")}),1.0]])]});
            var Q41;
            Q41=makeQuery(id+"F4.imprint","IMPRINT",FACE,{"disambiguationData":[TD([[makeQuery(id+"F4.imprint","IMPRINT",EDGE,{"derivedFrom":sQuery(id+"F4.wireOp",EDGE,"E52")}),1.0]])]});
            var Q42;
            Q42=makeQuery(id+"F4.imprint","IMPRINT",FACE,{"disambiguationData":[TD([[makeQuery(id+"F4.imprint","IMPRINT",EDGE,{"derivedFrom":sQuery(id+"F4.wireOp",EDGE,"E54")}),1.0]])]});
            var Q43;
            Q43=makeQuery(id+"F4.imprint","IMPRINT",FACE,{"disambiguationData":[TD([[makeQuery(id+"F4.imprint","IMPRINT",EDGE,{"derivedFrom":sQuery(id+"F4.wireOp",EDGE,"E55")}),1.0]])]});
            var Q44;
            Q44=makeQuery(id+"F4.imprint","IMPRINT",FACE,{"disambiguationData":[TD([[makeQuery(id+"F4.imprint","IMPRINT",EDGE,{"derivedFrom":sQuery(id+"F4.wireOp",EDGE,"E59")}),1.0]])]});
            var Q45;
            Q45=makeQuery(id+"F4.imprint","IMPRINT",FACE,{"disambiguationData":[TD([[makeQuery(id+"F4.imprint","IMPRINT",EDGE,{"derivedFrom":sQuery(id+"F4.wireOp",EDGE,"E61")}),1.0]])]});
            var Q46;
            Q46=makeQuery(id+"F4.imprint","IMPRINT",FACE,{"disambiguationData":[TD([[makeQuery(id+"F4.imprint","IMPRINT",EDGE,{"derivedFrom":sQuery(id+"F4.wireOp",EDGE,"E58")}),1.0]])]});
            var Q47;
            Q47=makeQuery(id+"F4.imprint","IMPRINT",FACE,{"disambiguationData":[TD([[makeQuery(id+"F4.imprint","IMPRINT",EDGE,{"derivedFrom":sQuery(id+"F4.wireOp",EDGE,"E67")}),1.0]])]});
            var Q48;
            Q48=makeQuery(id+"F4.imprint","IMPRINT",FACE,{"disambiguationData":[TD([[makeQuery(id+"F4.imprint","IMPRINT",EDGE,{"derivedFrom":sQuery(id+"F4.wireOp",EDGE,"E68")}),1.0]])]});
            var Q49;
            Q49=makeQuery(id+"F4.imprint","IMPRINT",FACE,{"disambiguationData":[TD([[makeQuery(id+"F4.imprint","IMPRINT",EDGE,{"derivedFrom":sQuery(id+"F4.wireOp",EDGE,"E63")}),1.0]])]});
            var Q50;
            Q50=makeQuery(id+"F4.imprint","IMPRINT",FACE,{"disambiguationData":[TD([[makeQuery(id+"F4.imprint","IMPRINT",EDGE,{"derivedFrom":sQuery(id+"F4.wireOp",EDGE,"E64")}),1.0]])]});
            var Q51;
            Q51=makeQuery(id+"F4.imprint","IMPRINT",FACE,{"disambiguationData":[TD([[makeQuery(id+"F4.imprint","IMPRINT",EDGE,{"derivedFrom":sQuery(id+"F4.wireOp",EDGE,"E30.19.0.1")}),1.0]])]});
            var Q52;
            Q52=makeQuery(id+"F4.imprint","IMPRINT",FACE,{"disambiguationData":[TD([[makeQuery(id+"F4.imprint","IMPRINT",EDGE,{"derivedFrom":sQuery(id+"F4.wireOp",EDGE,"E30.19.0.0")}),1.0]])]});
            var Q53;
            Q53=makeQuery(id+"F4.imprint","IMPRINT",FACE,{"disambiguationData":[TD([[makeQuery(id+"F4.imprint","IMPRINT",EDGE,{"derivedFrom":sQuery(id+"F4.wireOp",EDGE,"E30.18.0.0")}),1.0]])]});
            var Q54;
            Q54=makeQuery(id+"F4.imprint","IMPRINT",FACE,{"disambiguationData":[TD([[makeQuery(id+"F4.imprint","IMPRINT",EDGE,{"derivedFrom":sQuery(id+"F4.wireOp",EDGE,"E30.18.0.1")}),1.0]])]});
            var Q55;
            Q55=makeQuery(id+"F4.imprint","IMPRINT",FACE,{"disambiguationData":[TD([[makeQuery(id+"F4.imprint","IMPRINT",EDGE,{"derivedFrom":sQuery(id+"F4.wireOp",EDGE,"E30.17.0.0")}),1.0]])]});
            var Q56;
            Q56=makeQuery(id+"F4.imprint","IMPRINT",FACE,{"disambiguationData":[TD([[makeQuery(id+"F4.imprint","IMPRINT",EDGE,{"derivedFrom":sQuery(id+"F4.wireOp",EDGE,"E30.17.0.1")}),1.0]])]});
            var Q57;
            Q57=makeQuery(id+"F4.imprint","IMPRINT",FACE,{"disambiguationData":[TD([[makeQuery(id+"F4.imprint","IMPRINT",EDGE,{"derivedFrom":sQuery(id+"F4.wireOp",EDGE,"E30.16.0.0")}),1.0]])]});
            var Q58;
            Q58=makeQuery(id+"F4.imprint","IMPRINT",FACE,{"disambiguationData":[TD([[makeQuery(id+"F4.imprint","IMPRINT",EDGE,{"derivedFrom":sQuery(id+"F4.wireOp",EDGE,"E30.16.0.1")}),1.0]])]});
            var Q59;
            Q59=makeQuery(id+"F4.imprint","IMPRINT",FACE,{"disambiguationData":[TD([[makeQuery(id+"F4.imprint","IMPRINT",EDGE,{"derivedFrom":sQuery(id+"F4.wireOp",EDGE,"E30.15.0.0")}),1.0]])]});
            var Q60;
            Q60=makeQuery(id+"F4.imprint","IMPRINT",FACE,{"disambiguationData":[TD([[makeQuery(id+"F4.imprint","IMPRINT",EDGE,{"derivedFrom":sQuery(id+"F4.wireOp",EDGE,"E30.15.0.1")}),1.0]])]});
            var Q61;
            Q61=makeQuery(id+"F4.imprint","IMPRINT",FACE,{"disambiguationData":[TD([[makeQuery(id+"F4.imprint","IMPRINT",EDGE,{"derivedFrom":sQuery(id+"F4.wireOp",EDGE,"E30.14.0.0")}),1.0]])]});
            var Q62;
            Q62=makeQuery(id+"F4.imprint","IMPRINT",FACE,{"disambiguationData":[TD([[makeQuery(id+"F4.imprint","IMPRINT",EDGE,{"derivedFrom":sQuery(id+"F4.wireOp",EDGE,"E30.14.0.1")}),1.0]])]});
            var Q63;
            Q63=makeQuery(id+"F4.imprint","IMPRINT",FACE,{"disambiguationData":[TD([[makeQuery(id+"F4.imprint","IMPRINT",EDGE,{"derivedFrom":sQuery(id+"F4.wireOp",EDGE,"E30.13.0.0")}),1.0]])]});
            var Q64;
            Q64=makeQuery(id+"F4.imprint","IMPRINT",FACE,{"disambiguationData":[TD([[makeQuery(id+"F4.imprint","IMPRINT",EDGE,{"derivedFrom":sQuery(id+"F4.wireOp",EDGE,"E30.13.0.1")}),1.0]])]});
            var Q65;
            Q65=makeQuery(id+"F4.imprint","IMPRINT",FACE,{"disambiguationData":[TD([[makeQuery(id+"F4.imprint","IMPRINT",EDGE,{"derivedFrom":sQuery(id+"F4.wireOp",EDGE,"E30.12.0.0")}),1.0]])]});
            var Q66;
            Q66=makeQuery(id+"F4.imprint","IMPRINT",FACE,{"disambiguationData":[TD([[makeQuery(id+"F4.imprint","IMPRINT",EDGE,{"derivedFrom":sQuery(id+"F4.wireOp",EDGE,"E30.12.0.1")}),1.0]])]});
            var Q67;
            Q67=makeQuery(id+"F4.imprint","IMPRINT",FACE,{"disambiguationData":[TD([[makeQuery(id+"F4.imprint","IMPRINT",EDGE,{"derivedFrom":sQuery(id+"F4.wireOp",EDGE,"E30.11.0.0")}),1.0]])]});
            var Q68;
            Q68=makeQuery(id+"F4.imprint","IMPRINT",FACE,{"disambiguationData":[TD([[makeQuery(id+"F4.imprint","IMPRINT",EDGE,{"derivedFrom":sQuery(id+"F4.wireOp",EDGE,"E30.11.0.1")}),1.0]])]});
            var Q69;
            Q69=makeQuery(id+"F4.imprint","IMPRINT",FACE,{"disambiguationData":[TD([[makeQuery(id+"F4.imprint","IMPRINT",EDGE,{"derivedFrom":sQuery(id+"F4.wireOp",EDGE,"E30.10.0.0")}),1.0]])]});
            var Q70;
            Q70=makeQuery(id+"F4.imprint","IMPRINT",FACE,{"disambiguationData":[TD([[makeQuery(id+"F4.imprint","IMPRINT",EDGE,{"derivedFrom":sQuery(id+"F4.wireOp",EDGE,"E30.10.0.1")}),1.0]])]});
            var Q71;
            Q71=makeQuery(id+"F4.imprint","IMPRINT",FACE,{"disambiguationData":[TD([[makeQuery(id+"F4.imprint","IMPRINT",EDGE,{"derivedFrom":sQuery(id+"F4.wireOp",EDGE,"E30.9.0.0")}),1.0]])]});
            var Q72;
            Q72=makeQuery(id+"F4.imprint","IMPRINT",FACE,{"disambiguationData":[TD([[makeQuery(id+"F4.imprint","IMPRINT",EDGE,{"derivedFrom":sQuery(id+"F4.wireOp",EDGE,"E30.9.0.1")}),1.0]])]});
            var Q73;
            Q73=makeQuery(id+"F4.imprint","IMPRINT",FACE,{"disambiguationData":[TD([[makeQuery(id+"F4.imprint","IMPRINT",EDGE,{"derivedFrom":sQuery(id+"F4.wireOp",EDGE,"E30.8.0.0")}),1.0]])]});
            var Q74;
            Q74=makeQuery(id+"F4.imprint","IMPRINT",FACE,{"disambiguationData":[TD([[makeQuery(id+"F4.imprint","IMPRINT",EDGE,{"derivedFrom":sQuery(id+"F4.wireOp",EDGE,"E30.8.0.1")}),1.0]])]});
            var Q75;
            Q75=makeQuery(id+"F4.imprint","IMPRINT",FACE,{"disambiguationData":[TD([[makeQuery(id+"F4.imprint","IMPRINT",EDGE,{"derivedFrom":sQuery(id+"F4.wireOp",EDGE,"E30.7.0.0")}),1.0]])]});
            var Q76;
            Q76=makeQuery(id+"F4.imprint","IMPRINT",FACE,{"disambiguationData":[TD([[makeQuery(id+"F4.imprint","IMPRINT",EDGE,{"derivedFrom":sQuery(id+"F4.wireOp",EDGE,"E30.7.0.1")}),1.0]])]});
            var Q77;
            Q77=makeQuery(id+"F4.imprint","IMPRINT",FACE,{"disambiguationData":[TD([[makeQuery(id+"F4.imprint","IMPRINT",EDGE,{"derivedFrom":sQuery(id+"F4.wireOp",EDGE,"E30.6.0.0")}),1.0]])]});
            var Q78;
            Q78=makeQuery(id+"F4.imprint","IMPRINT",FACE,{"disambiguationData":[TD([[makeQuery(id+"F4.imprint","IMPRINT",EDGE,{"derivedFrom":sQuery(id+"F4.wireOp",EDGE,"E30.6.0.1")}),1.0]])]});
            var Q79;
            Q79=makeQuery(id+"F4.imprint","IMPRINT",FACE,{"disambiguationData":[TD([[makeQuery(id+"F4.imprint","IMPRINT",EDGE,{"derivedFrom":sQuery(id+"F4.wireOp",EDGE,"E30.5.0.0")}),1.0]])]});
            var Q80;
            Q80=makeQuery(id+"F4.imprint","IMPRINT",FACE,{"disambiguationData":[TD([[makeQuery(id+"F4.imprint","IMPRINT",EDGE,{"derivedFrom":sQuery(id+"F4.wireOp",EDGE,"E30.5.0.1")}),1.0]])]});
            var Q81;
            Q81=makeQuery(id+"F4.imprint","IMPRINT",FACE,{"disambiguationData":[TD([[makeQuery(id+"F4.imprint","IMPRINT",EDGE,{"derivedFrom":sQuery(id+"F4.wireOp",EDGE,"E30.4.0.0")}),1.0]])]});
            var Q82;
            Q82=makeQuery(id+"F4.imprint","IMPRINT",FACE,{"disambiguationData":[TD([[makeQuery(id+"F4.imprint","IMPRINT",EDGE,{"derivedFrom":sQuery(id+"F4.wireOp",EDGE,"E30.4.0.1")}),1.0]])]});
            var Q83;
            Q83=makeQuery(id+"F4.imprint","IMPRINT",FACE,{"disambiguationData":[TD([[makeQuery(id+"F4.imprint","IMPRINT",EDGE,{"derivedFrom":sQuery(id+"F4.wireOp",EDGE,"E30.3.0.0")}),1.0]])]});
            var Q84;
            Q84=makeQuery(id+"F4.imprint","IMPRINT",FACE,{"disambiguationData":[TD([[makeQuery(id+"F4.imprint","IMPRINT",EDGE,{"derivedFrom":sQuery(id+"F4.wireOp",EDGE,"E30.3.0.1")}),1.0]])]});
            var Q85;
            Q85=makeQuery(id+"F4.imprint","IMPRINT",FACE,{"disambiguationData":[TD([[makeQuery(id+"F4.imprint","IMPRINT",EDGE,{"derivedFrom":sQuery(id+"F4.wireOp",EDGE,"E30.2.0.0")}),1.0]])]});
            var Q86;
            Q86=makeQuery(id+"F4.imprint","IMPRINT",FACE,{"disambiguationData":[TD([[makeQuery(id+"F4.imprint","IMPRINT",EDGE,{"derivedFrom":sQuery(id+"F4.wireOp",EDGE,"E30.2.0.1")}),1.0]])]});
            var Q87;
            Q87=makeQuery(id+"F4.imprint","IMPRINT",FACE,{"disambiguationData":[TD([[makeQuery(id+"F4.imprint","IMPRINT",EDGE,{"derivedFrom":sQuery(id+"F4.wireOp",EDGE,"E30.1.0.0")}),1.0]])]});
            var Q88;
            Q88=makeQuery(id+"F4.imprint","IMPRINT",FACE,{"disambiguationData":[TD([[makeQuery(id+"F4.imprint","IMPRINT",EDGE,{"derivedFrom":sQuery(id+"F4.wireOp",EDGE,"E30.1.0.1")}),1.0]])]});
            var Q89;
            Q89=makeQuery(id+"F4.imprint","IMPRINT",FACE,{"disambiguationData":[TD([[makeQuery(id+"F4.imprint","IMPRINT",EDGE,{"derivedFrom":sQuery(id+"F4.wireOp",EDGE,"E28")}),1.0]])]});
            var Q90;
            Q90=makeQuery(id+"F4.imprint","IMPRINT",FACE,{"disambiguationData":[TD([[makeQuery(id+"F4.imprint","IMPRINT",EDGE,{"derivedFrom":sQuery(id+"F4.wireOp",EDGE,"E29")}),1.0]])]});
            extrude(context, id + "F5", {"entities" : qUnion([Q0, Q1, Q2, Q3, Q4, Q5, Q6, Q7, Q8, Q9, Q10, Q11, Q12, Q13, Q14, Q15, Q16, Q17, Q18, Q19, Q20, Q21, Q22, Q23, Q24, Q25, Q26, Q27, Q28, Q29, Q30, Q31, Q32, Q33, Q34, Q35, Q36, Q37, Q38, Q39, Q40, Q41, Q42, Q43, Q44, Q45, Q46, Q47, Q48, Q49, Q50, Q51, Q52, Q53, Q54, Q55, Q56, Q57, Q58, Q59, Q60, Q61, Q62, Q63, Q64, Q65, Q66, Q67, Q68, Q69, Q70, Q71, Q72, Q73, Q74, Q75, Q76, Q77, Q78, Q79, Q80, Q81, Q82, Q83, Q84, Q85, Q86, Q87, Q88, Q89, Q90]), "operationType" : NewBodyOperationType.REMOVE, "endBound" : BoundingType.THROUGH_ALL, "oppositeDirection" : true, "depth" : 25 * mm, "offsetDistance" : 25 * mm});
        }
        {
            var Q0;
            Q0=makeQuery(id+"F4.imprint","IMPRINT",FACE,{"disambiguationData":[TD([[makeQuery(id+"F4.imprint","IMPRINT",EDGE,{"derivedFrom":sQuery(id+"F4.wireOp",EDGE,"E21.bottom")}),-1.0]])]});
            var Q1;
            Q1=makeQuery(id+"F4.imprint","IMPRINT",FACE,{"disambiguationData":[TD([[makeQuery(id+"F4.imprint","IMPRINT",EDGE,{"derivedFrom":sQuery(id+"F4.wireOp",EDGE,"E38.1.0.6")}),-1.0]])]});
            var Q2;
            Q2=makeQuery(id+"F4.imprint","IMPRINT",FACE,{"disambiguationData":[TD([[makeQuery(id+"F4.imprint","IMPRINT",EDGE,{"derivedFrom":sQuery(id+"F4.wireOp",EDGE,"E39.bottom")}),-1.0]])]});
            var Q3;
            Q3=makeQuery(id+"F4.imprint","IMPRINT",FACE,{"disambiguationData":[TD([[makeQuery(id+"F4.imprint","IMPRINT",EDGE,{"derivedFrom":sQuery(id+"F4.wireOp",EDGE,"E51.0.1.3")}),1.0]])]});
            var Q4;
            Q4=makeQuery(id+"F4.imprint","IMPRINT",FACE,{"disambiguationData":[TD([[makeQuery(id+"F4.imprint","IMPRINT",EDGE,{"derivedFrom":sQuery(id+"F4.wireOp",EDGE,"E38.1.1.6")}),-1.0]])]});
            var Q5;
            Q5=makeQuery(id+"F4.imprint","IMPRINT",FACE,{"disambiguationData":[TD([[makeQuery(id+"F4.imprint","IMPRINT",EDGE,{"derivedFrom":sQuery(id+"F4.wireOp",EDGE,"E38.0.1.6")}),-1.0]])]});
            var Q6;
            Q6=makeQuery(id+"F4.imprint","IMPRINT",FACE,{"disambiguationData":[TD([[makeQuery(id+"F4.imprint","IMPRINT",EDGE,{"derivedFrom":sQuery(id+"F4.wireOp",EDGE,"E22.bottom")}),-1.0]])]});
            var Q7;
            Q7=makeQuery(id+"F4.imprint","IMPRINT",FACE,{"disambiguationData":[TD([[makeQuery(id+"F4.imprint","IMPRINT",EDGE,{"derivedFrom":sQuery(id+"F4.wireOp",EDGE,"E57.bottom")}),-1.0]])]});
            var Q8;
            Q8=makeQuery(id+"F4.imprint","IMPRINT",FACE,{"disambiguationData":[TD([[makeQuery(id+"F4.imprint","IMPRINT",EDGE,{"derivedFrom":sQuery(id+"F4.wireOp",EDGE,"E23")}),1.0]])]});
            var Q9;
            Q9=makeQuery(id+"F4.imprint","IMPRINT",FACE,{"disambiguationData":[TD([[makeQuery(id+"F4.imprint","IMPRINT",EDGE,{"derivedFrom":sQuery(id+"F4.wireOp",EDGE,"E65")}),1.0]])]});
            extrude(context, id + "F6", {"entities" : qUnion([Q0, Q1, Q2, Q3, Q4, Q5, Q6, Q7, Q8, Q9]), "operationType" : NewBodyOperationType.REMOVE, "oppositeDirection" : true, "depth" : 0.1 * mm, "offsetDistance" : 25 * mm});
        }
        {
            var Q0;
            Q0=makeQuery(id+"F1.opExtrude","CAP_FACE",FACE,{"disambiguationData":[OSD([sQuery(id+"F0.wireOp",EDGE,"E0.bottom"),sQuery(id+"F0.wireOp",EDGE,"E0.top"),sQuery(id+"F0.wireOp",EDGE,"E0.left"),sQuery(id+"F0.wireOp",EDGE,"E5"),sQuery(id+"F0.wireOp",EDGE,"E6"),sQuery(id+"F0.wireOp",EDGE,"E7"),sQuery(id+"F0.wireOp",EDGE,"E8"),sQuery(id+"F0.wireOp",EDGE,"E9"),sQuery(id+"F0.wireOp",EDGE,"E10.bottom"),sQuery(id+"F0.wireOp",EDGE,"E10.top"),sQuery(id+"F0.wireOp",EDGE,"E10.left"),sQuery(id+"F0.wireOp",EDGE,"E10.right")])],"isStart":true});
            var sketch = newSketch(context, id + "F7", { "sketchPlane" : qUnion([Q0])});
            skLineSegment(sketch, "E69.bottom", {"start": v(-25.65, -27.04) * mm, "end": v(25.65, -27.04) * mm});
            skLineSegment(sketch, "E69.top", {"start": v(-25.65, -22.04) * mm, "end": v(25.65, -22.04) * mm});
            skLineSegment(sketch, "E69.left", {"start": v(-25.65, -27.04) * mm, "end": v(-25.65, -22.04) * mm});
            skLineSegment(sketch, "E69.right", {"start": v(25.65, -27.04) * mm, "end": v(25.65, -22.04) * mm});
            skLineSegment(sketch, "E70", {"start": v(0, -22.04) * mm, "end": v(0, -27.04) * mm, "construction": true});
            skPoint(sketch, "E71", {"position": v(-29, -24.54) * mm});
            skLineSegment(sketch, "E72", {"start": v(-25.65, -24.54) * mm, "end": v(25.65, -24.54) * mm, "construction": true});
            skCircle(sketch, "E73", {"center": v(24.1, -23.25) * mm, "radius": 0.75 * mm});
            skCircle(sketch, "E74", {"center": v(24.1, -25.79) * mm, "radius": 0.75 * mm});
            skCircle(sketch, "E75.1.0.0", {"center": v(21.57, -23.25) * mm, "radius": 0.75 * mm});
            skCircle(sketch, "E75.1.0.1", {"center": v(21.57, -25.79) * mm, "radius": 0.75 * mm});
            skCircle(sketch, "E75.2.0.0", {"center": v(19.03, -23.25) * mm, "radius": 0.75 * mm});
            skCircle(sketch, "E75.2.0.1", {"center": v(19.03, -25.79) * mm, "radius": 0.75 * mm});
            skCircle(sketch, "E75.3.0.0", {"center": v(16.49, -23.25) * mm, "radius": 0.75 * mm});
            skCircle(sketch, "E75.3.0.1", {"center": v(16.49, -25.79) * mm, "radius": 0.75 * mm});
            skCircle(sketch, "E75.4.0.0", {"center": v(13.95, -23.25) * mm, "radius": 0.75 * mm});
            skCircle(sketch, "E75.4.0.1", {"center": v(13.95, -25.79) * mm, "radius": 0.75 * mm});
            skCircle(sketch, "E75.5.0.0", {"center": v(11.4, -23.25) * mm, "radius": 0.75 * mm});
            skCircle(sketch, "E75.5.0.1", {"center": v(11.4, -25.79) * mm, "radius": 0.75 * mm});
            skCircle(sketch, "E75.6.0.0", {"center": v(8.87, -23.25) * mm, "radius": 0.75 * mm});
            skCircle(sketch, "E75.6.0.1", {"center": v(8.87, -25.79) * mm, "radius": 0.75 * mm});
            skCircle(sketch, "E75.7.0.0", {"center": v(6.33, -23.25) * mm, "radius": 0.75 * mm});
            skCircle(sketch, "E75.7.0.1", {"center": v(6.33, -25.79) * mm, "radius": 0.75 * mm});
            skCircle(sketch, "E75.8.0.0", {"center": v(3.79, -23.25) * mm, "radius": 0.75 * mm});
            skCircle(sketch, "E75.8.0.1", {"center": v(3.79, -25.79) * mm, "radius": 0.75 * mm});
            skCircle(sketch, "E75.9.0.0", {"center": v(1.25, -23.25) * mm, "radius": 0.75 * mm});
            skCircle(sketch, "E75.9.0.1", {"center": v(1.25, -25.79) * mm, "radius": 0.75 * mm});
            skCircle(sketch, "E75.10.0.0", {"center": v(-1.3, -23.25) * mm, "radius": 0.75 * mm});
            skCircle(sketch, "E75.10.0.1", {"center": v(-1.3, -25.79) * mm, "radius": 0.75 * mm});
            skCircle(sketch, "E75.11.0.0", {"center": v(-3.83, -23.25) * mm, "radius": 0.75 * mm});
            skCircle(sketch, "E75.11.0.1", {"center": v(-3.83, -25.79) * mm, "radius": 0.75 * mm});
            skCircle(sketch, "E75.12.0.0", {"center": v(-6.37, -23.25) * mm, "radius": 0.75 * mm});
            skCircle(sketch, "E75.12.0.1", {"center": v(-6.37, -25.8) * mm, "radius": 0.75 * mm});
            skCircle(sketch, "E75.13.0.0", {"center": v(-8.91, -23.25) * mm, "radius": 0.75 * mm});
            skCircle(sketch, "E75.13.0.1", {"center": v(-8.91, -25.8) * mm, "radius": 0.75 * mm});
            skCircle(sketch, "E75.14.0.0", {"center": v(-11.45, -23.25) * mm, "radius": 0.75 * mm});
            skCircle(sketch, "E75.14.0.1", {"center": v(-11.45, -25.8) * mm, "radius": 0.75 * mm});
            skCircle(sketch, "E75.15.0.0", {"center": v(-14, -23.25) * mm, "radius": 0.75 * mm});
            skCircle(sketch, "E75.15.0.1", {"center": v(-14, -25.8) * mm, "radius": 0.75 * mm});
            skCircle(sketch, "E75.16.0.0", {"center": v(-16.53, -23.25) * mm, "radius": 0.75 * mm});
            skCircle(sketch, "E75.16.0.1", {"center": v(-16.53, -25.8) * mm, "radius": 0.75 * mm});
            skCircle(sketch, "E75.17.0.0", {"center": v(-19.07, -23.25) * mm, "radius": 0.75 * mm});
            skCircle(sketch, "E75.17.0.1", {"center": v(-19.07, -25.8) * mm, "radius": 0.75 * mm});
            skCircle(sketch, "E75.18.0.0", {"center": v(-21.61, -23.25) * mm, "radius": 0.75 * mm});
            skCircle(sketch, "E75.18.0.1", {"center": v(-21.61, -25.8) * mm, "radius": 0.75 * mm});
            skCircle(sketch, "E75.19.0.0", {"center": v(-24.15, -23.25) * mm, "radius": 0.75 * mm});
            skCircle(sketch, "E75.19.0.1", {"center": v(-24.15, -25.8) * mm, "radius": 0.75 * mm});
            skLineSegment(sketch, "E75.direction1", {"start": v(24.1, -23.25) * mm, "end": v(21.57, -23.25) * mm, "construction": true});
            skPoint(sketch, "E76", {"position": v(24.1, -25.8) * mm});
            skSolve(sketch);
        }
        {
            var Q0;
            Q0=makeQuery(id+"F7.imprint","IMPRINT",FACE,{"disambiguationData":[TD([[makeQuery(id+"F7.imprint","IMPRINT",EDGE,{"derivedFrom":sQuery(id+"F7.wireOp",EDGE,"E69.bottom")}),1.0]])]});
            extrude(context, id + "F8", {"entities" : qUnion([Q0]), "operationType" : NewBodyOperationType.REMOVE, "oppositeDirection" : true, "depth" : 0.1 * mm, "offsetDistance" : 25 * mm});
        }
    });
